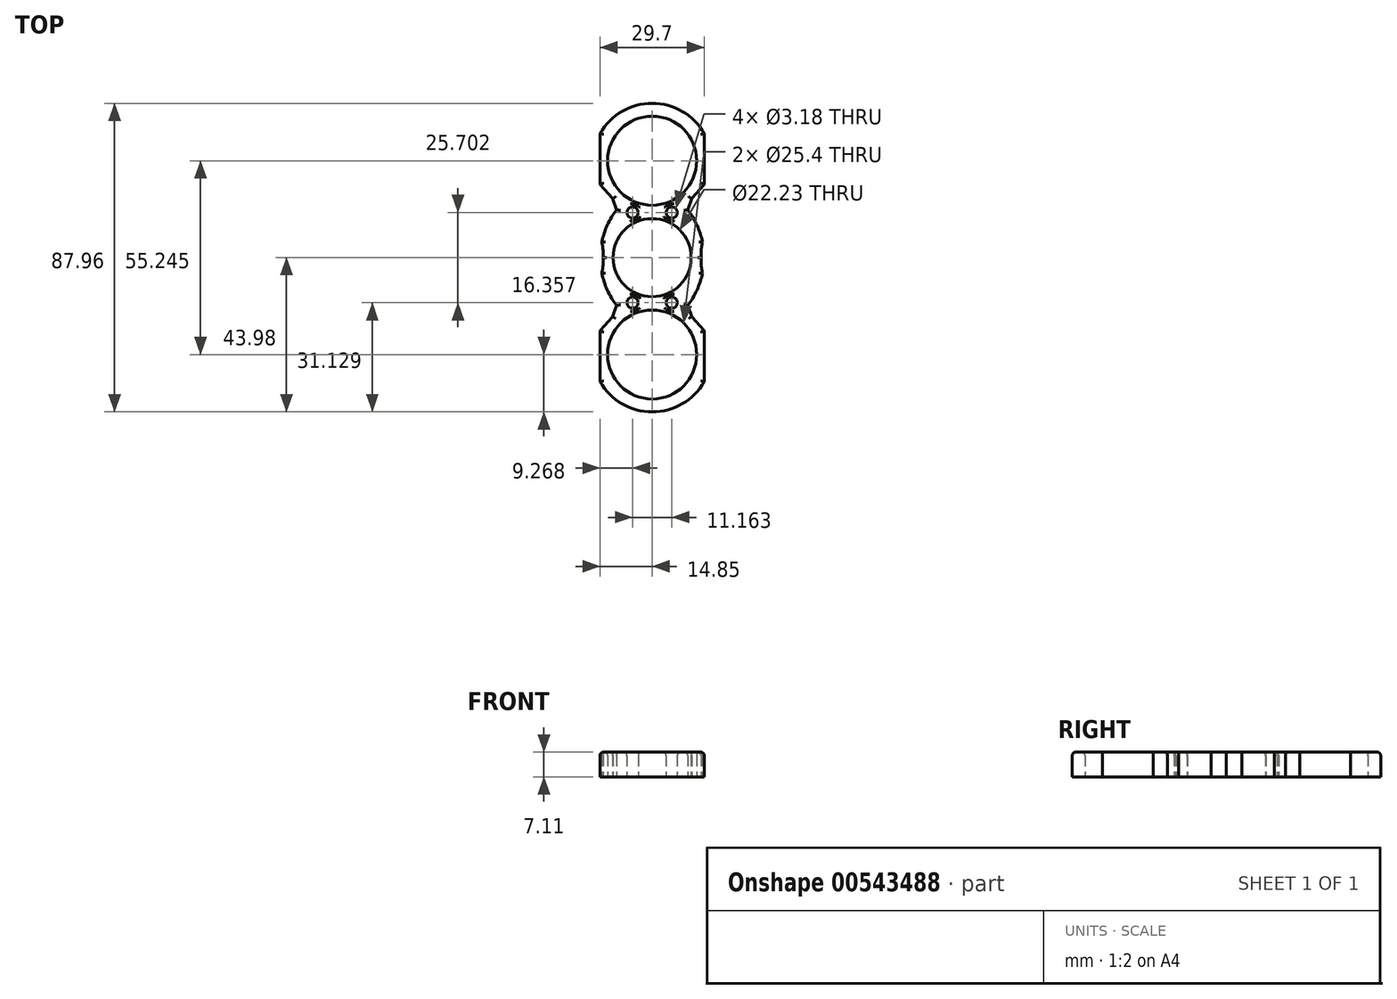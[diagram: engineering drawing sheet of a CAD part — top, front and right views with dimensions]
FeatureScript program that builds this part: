
annotation { "Feature Type Name" : "Feature", "Feature Type Description" : "" }
export const myFeature = defineFeature(function(context is Context, id is Id, definition is map)
    precondition{}
    {
        {
            var Q0;
            Q0=qCreatedBy(makeId("Top.planeOp"),FACE);
            var sketch = newSketch(context, id + "F0", { "sketchPlane" : qUnion([Q0])});
            skCircle(sketch, "E0", {"center": v(0, 0) * mm, "radius": 11.11 * mm});
            skCircle(sketch, "E1", {"center": v(0, 27.62) * mm, "radius": 12.7 * mm});
            skCircle(sketch, "E2", {"center": v(0, -27.62) * mm, "radius": 12.7 * mm});
            skLineSegment(sketch, "E3", {"start": v(-6, 42.55) * mm, "end": v(-5.71, 42.55) * mm});
            skLineSegment(sketch, "E4", {"start": v(14.85, 35.41) * mm, "end": v(14.85, 20.85) * mm});
            skLineSegment(sketch, "E5", {"start": v(14.85, 20.85) * mm, "end": v(11.28, 16.85) * mm});
            skLineSegment(sketch, "E6", {"start": v(-56.83, 0) * mm, "end": v(-12.8, 0) * mm});
            skLineSegment(sketch, "E7", {"start": v(0, 64.82) * mm, "end": v(0, -65.68) * mm});
            skLineSegment(sketch, "E8.MirrorCS", {"start": v(-6, -42.55) * mm, "end": v(-5.71, -42.55) * mm});
            skLineSegment(sketch, "E9.MirrorCS", {"start": v(14.85, -35.41) * mm, "end": v(14.85, -20.85) * mm});
            skLineSegment(sketch, "E10.MirrorCS", {"start": v(14.85, -20.85) * mm, "end": v(11.28, -16.85) * mm});
            skLineSegment(sketch, "E11.MirrorCS", {"start": v(-14.85, 35.41) * mm, "end": v(-14.85, 20.85) * mm});
            skLineSegment(sketch, "E12.MirrorCS", {"start": v(-14.85, 20.85) * mm, "end": v(-11.28, 16.85) * mm});
            skLineSegment(sketch, "E13.MirrorCS", {"start": v(-14.85, -20.85) * mm, "end": v(-11.28, -16.85) * mm});
            skLineSegment(sketch, "E14.MirrorCS", {"start": v(-14.85, -35.41) * mm, "end": v(-14.85, -20.85) * mm});
            skPoint(sketch, "E15.MirrorCS.end.orphan", {"position": v(-14.85, -35.41) * mm});
            skPoint(sketch, "E15.MirrorCS.start.orphan", {"position": v(-5.71, -42.55) * mm});
            skPoint(sketch, "E16.trimOffspring.end.orphan", {"position": v(5.71, -42.55) * mm});
            skPoint(sketch, "E17.MirrorCS.end.orphan", {"position": v(14.85, -35.41) * mm});
            skArc(sketch, "E18", {"start": v(-14.85, -35.41) * mm, "mid": v(0, -43.98) * mm, "end": v(14.85, -35.41) * mm});
            skPoint(sketch, "E19.MirrorCS.end.orphan", {"position": v(-14.85, 35.41) * mm});
            skPoint(sketch, "E19.MirrorCS.start.orphan", {"position": v(-5.71, 42.55) * mm});
            skPoint(sketch, "E20.start.orphan", {"position": v(5.71, 42.55) * mm});
            skArc(sketch, "E21.MirrorCS", {"start": v(-14.85, 35.41) * mm, "mid": v(0, 43.98) * mm, "end": v(14.85, 35.41) * mm});
            skPoint(sketch, "E22.orphan", {"position": v(-14.85, 0) * mm});
            skPoint(sketch, "E23.orphan", {"position": v(14.85, 0) * mm});
            skLineSegment(sketch, "E24", {"start": v(11.28, 16.85) * mm, "end": v(10.16, 13.64) * mm});
            skLineSegment(sketch, "E25.MirrorCS", {"start": v(-11.28, 16.85) * mm, "end": v(-10.16, 13.64) * mm});
            skPoint(sketch, "E26.orphan", {"position": v(-7.71, 12.85) * mm});
            skPoint(sketch, "E27.orphan", {"position": v(7.71, 12.85) * mm});
            skLineSegment(sketch, "E28.MirrorCS", {"start": v(-11.28, -16.85) * mm, "end": v(-10.16, -13.64) * mm});
            skLineSegment(sketch, "E29.MirrorCS", {"start": v(11.28, -16.85) * mm, "end": v(10.16, -13.64) * mm});
            skPoint(sketch, "E30.orphan", {"position": v(-7.71, -12.85) * mm});
            skPoint(sketch, "E31.orphan", {"position": v(7.71, -12.85) * mm});
            skCircle(sketch, "E32", {"center": v(-5.58, 12.85) * mm, "radius": 1.59 * mm});
            skCircle(sketch, "E33.MirrorC", {"center": v(-5.58, -12.85) * mm, "radius": 1.59 * mm});
            skCircle(sketch, "E34.MirrorC", {"center": v(5.58, 12.85) * mm, "radius": 1.59 * mm});
            skCircle(sketch, "E35.MirrorC", {"center": v(5.58, -12.85) * mm, "radius": 1.59 * mm});
            skPoint(sketch, "E36.orphan", {"position": v(-13.27, -35.21) * mm});
            skPoint(sketch, "E37.end.orphan", {"position": v(13.09, -35.41) * mm});
            skPoint(sketch, "E38.orphan", {"position": v(-13.27, 35.21) * mm});
            skPoint(sketch, "E39.MirrorCS.end.orphan", {"position": v(13.09, 35.41) * mm});
            skLineSegment(sketch, "E40.trimOffspring", {"start": v(-11.11, 0) * mm, "end": v(65.4, 0) * mm});
            skPoint(sketch, "E41.end.orphan", {"position": v(-12.8, -3.68) * mm});
            skPoint(sketch, "E42.MirrorCS.end.orphan", {"position": v(-12.8, 3.68) * mm});
            skPoint(sketch, "E43.orphan", {"position": v(12.8, -3.68) * mm});
            skPoint(sketch, "E44.end.orphan", {"position": v(12.8, 3.68) * mm});
            skArc(sketch, "E45", {"start": v(-10.16, 13.64) * mm, "mid": v(-12.78, 9.26) * mm, "end": v(-14.34, 4.4) * mm});
            skArc(sketch, "E46.MirrorCS", {"start": v(10.16, 13.64) * mm, "mid": v(12.78, 9.26) * mm, "end": v(14.34, 4.4) * mm});
            skPoint(sketch, "E47.orphan", {"position": v(-9.05, 10.44) * mm});
            skPoint(sketch, "E48.orphan", {"position": v(-9.05, -10.44) * mm});
            skPoint(sketch, "E49.orphan", {"position": v(9.05, -10.44) * mm});
            skPoint(sketch, "E50.MirrorCS.start.orphan", {"position": v(9.05, 10.44) * mm});
            skArc(sketch, "E51", {"start": v(-13.94, 0) * mm, "mid": v(-14.01, 2.21) * mm, "end": v(-14.34, 4.4) * mm});
            skArc(sketch, "E52.MirrorCS", {"start": v(-13.94, 0) * mm, "mid": v(-14.01, -2.21) * mm, "end": v(-14.34, -4.4) * mm});
            skArc(sketch, "E53.MirrorCS", {"start": v(13.94, 0) * mm, "mid": v(14.01, 2.21) * mm, "end": v(14.34, 4.4) * mm});
            skArc(sketch, "E54.MirrorCS", {"start": v(13.94, 0) * mm, "mid": v(14.01, -2.21) * mm, "end": v(14.34, -4.4) * mm});
            skArc(sketch, "E55.trimOffspring", {"start": v(-14.34, -4.4) * mm, "mid": v(-12.78, -9.26) * mm, "end": v(-10.16, -13.64) * mm});
            skArc(sketch, "E56.trimOffspring", {"start": v(14.34, -4.4) * mm, "mid": v(12.78, -9.26) * mm, "end": v(10.16, -13.64) * mm});
            skSolve(sketch);
        }
        {
            var Q0;
            {var subQ11=sQuery(id+"F0.wireOp",EDGE,"E11.MirrorCS");Q0=makeQuery(id+"F0.imprint","IMPRINT",FACE,{"disambiguationData":[TD([[makeQuery(id+"F0.imprint","IMPRINT",EDGE,{"derivedFrom":subQ11}),1.0]])]});}
            var Q1;
            {var subQ1=sQuery(id+"F0.wireOp",EDGE,"E4");Q1=makeQuery(id+"F0.imprint","IMPRINT",FACE,{"disambiguationData":[TD([[makeQuery(id+"F0.imprint","IMPRINT",EDGE,{"derivedFrom":subQ1}),-1.0]])]});}
            var Q2;
            {var subQ1=sQuery(id+"F0.wireOp",EDGE,"ecd911c1-05eb-48ea-925a-85692354c2d40.MirrorCS");Q2=makeQuery(id+"F0.imprint","IMPRINT",FACE,{"disambiguationData":[TD([[makeQuery(id+"F0.imprint","IMPRINT",EDGE,{"derivedFrom":subQ1}),-1.0]])]});}
            var Q3;
            {var subQ4=sQuery(id+"F0.wireOp",EDGE,"E9.MirrorCS");Q3=makeQuery(id+"F0.imprint","IMPRINT",FACE,{"disambiguationData":[TD([[makeQuery(id+"F0.imprint","IMPRINT",EDGE,{"derivedFrom":subQ4}),1.0]])]});}
            extrude(context, id + "F1", {"entities" : qUnion([Q0, Q1, Q2, Q3]), "depth" : 7.11 * mm, "offsetDistance" : 25.4 * mm});
        }
        {
            var Q0;
            Q0=makeQuery(id+"F1.opExtrude","CAP_EDGE",EDGE,{"disambiguationData":[OSD([sQuery(id+"F0.wireOp",EDGE,"E21.MirrorCS")])],"isStart":false});
            var Q1;
            Q1=makeQuery(id+"F1.opExtrude","CAP_EDGE",EDGE,{"disambiguationData":[OSD([sQuery(id+"F0.wireOp",EDGE,"E11.MirrorCS")])],"isStart":false});
            var Q2;
            Q2=makeQuery(id+"F1.opExtrude","CAP_EDGE",EDGE,{"disambiguationData":[OSD([sQuery(id+"F0.wireOp",EDGE,"E4")])],"isStart":false});
            var Q3;
            Q3=makeQuery(id+"F1.opExtrude","CAP_EDGE",EDGE,{"disambiguationData":[OSD([sQuery(id+"F0.wireOp",EDGE,"E12.MirrorCS")])],"isStart":false});
            var Q4;
            Q4=makeQuery(id+"F1.opExtrude","CAP_EDGE",EDGE,{"disambiguationData":[OSD([sQuery(id+"F0.wireOp",EDGE,"E25.MirrorCS")])],"isStart":false});
            var Q5;
            Q5=makeQuery(id+"F1.opExtrude","CAP_EDGE",EDGE,{"disambiguationData":[OSD([sQuery(id+"F0.wireOp",EDGE,"E42.MirrorCS")])],"isStart":false});
            var Q6;
            Q6=makeQuery(id+"F1.opExtrude","CAP_EDGE",EDGE,{"disambiguationData":[OSD([sQuery(id+"F0.wireOp",EDGE,"E24")])],"isStart":false});
            var Q7;
            Q7=makeQuery(id+"F1.opExtrude","CAP_EDGE",EDGE,{"disambiguationData":[OSD([sQuery(id+"F0.wireOp",EDGE,"E5")])],"isStart":false});
            var Q8;
            Q8=makeQuery(id+"F1.opExtrude","CAP_EDGE",EDGE,{"disambiguationData":[OSD([sQuery(id+"F0.wireOp",EDGE,"E44")])],"isStart":false});
            var Q9;
            Q9=makeQuery(id+"F1.opExtrude","CAP_EDGE",EDGE,{"disambiguationData":[OSD([sQuery(id+"F0.wireOp",EDGE,"481f827d-7c93-4f8f-ba0d-fe1300a66f5e0.MirrorCS")])],"isStart":false});
            var Q10;
            Q10=makeQuery(id+"F1.opExtrude","CAP_EDGE",EDGE,{"disambiguationData":[OSD([sQuery(id+"F0.wireOp",EDGE,"E41")])],"isStart":false});
            var Q11;
            Q11=makeQuery(id+"F1.opExtrude","CAP_EDGE",EDGE,{"disambiguationData":[OSD([sQuery(id+"F0.wireOp",EDGE,"ecd911c1-05eb-48ea-925a-85692354c2d40.MirrorCS")])],"isStart":false});
            var Q12;
            Q12=makeQuery(id+"F1.opExtrude","CAP_EDGE",EDGE,{"disambiguationData":[OSD([sQuery(id+"F0.wireOp",EDGE,"E28.MirrorCS")])],"isStart":false});
            var Q13;
            Q13=makeQuery(id+"F1.opExtrude","CAP_EDGE",EDGE,{"disambiguationData":[OSD([sQuery(id+"F0.wireOp",EDGE,"E13.MirrorCS")])],"isStart":false});
            var Q14;
            Q14=makeQuery(id+"F1.opExtrude","CAP_EDGE",EDGE,{"disambiguationData":[OSD([sQuery(id+"F0.wireOp",EDGE,"E14.MirrorCS")])],"isStart":false});
            var Q15;
            Q15=makeQuery(id+"F1.opExtrude","CAP_EDGE",EDGE,{"disambiguationData":[OSD([sQuery(id+"F0.wireOp",EDGE,"E29.MirrorCS")])],"isStart":false});
            var Q16;
            Q16=makeQuery(id+"F1.opExtrude","CAP_EDGE",EDGE,{"disambiguationData":[OSD([sQuery(id+"F0.wireOp",EDGE,"f6da66dd-6fcb-4a6b-93cb-794cc1521f9f0.MirrorCS")])],"isStart":false});
            var Q17;
            Q17=makeQuery(id+"F1.opExtrude","CAP_EDGE",EDGE,{"disambiguationData":[OSD([sQuery(id+"F0.wireOp",EDGE,"E10.MirrorCS")])],"isStart":false});
            var Q18;
            Q18=makeQuery(id+"F1.opExtrude","CAP_EDGE",EDGE,{"disambiguationData":[OSD([sQuery(id+"F0.wireOp",EDGE,"E9.MirrorCS")])],"isStart":false});
            var Q19;
            Q19=makeQuery(id+"F1.opExtrude","CAP_EDGE",EDGE,{"disambiguationData":[OSD([sQuery(id+"F0.wireOp",EDGE,"E18")])],"isStart":false});
            var Q20;
            Q20=makeQuery(id+"F1.opExtrude","CAP_EDGE",EDGE,{"disambiguationData":[OSD([sQuery(id+"F0.wireOp",EDGE,"E21.MirrorCS")])],"isStart":true});
            var Q21;
            Q21=makeQuery(id+"F1.opExtrude","CAP_EDGE",EDGE,{"disambiguationData":[OSD([sQuery(id+"F0.wireOp",EDGE,"E4")])],"isStart":true});
            var Q22;
            Q22=makeQuery(id+"F1.opExtrude","CAP_EDGE",EDGE,{"disambiguationData":[OSD([sQuery(id+"F0.wireOp",EDGE,"E11.MirrorCS")])],"isStart":true});
            var Q23;
            Q23=makeQuery(id+"F1.opExtrude","CAP_EDGE",EDGE,{"disambiguationData":[OSD([sQuery(id+"F0.wireOp",EDGE,"E12.MirrorCS")])],"isStart":true});
            var Q24;
            Q24=makeQuery(id+"F1.opExtrude","CAP_EDGE",EDGE,{"disambiguationData":[OSD([sQuery(id+"F0.wireOp",EDGE,"E25.MirrorCS")])],"isStart":true});
            var Q25;
            Q25=makeQuery(id+"F1.opExtrude","CAP_EDGE",EDGE,{"disambiguationData":[OSD([sQuery(id+"F0.wireOp",EDGE,"E42.MirrorCS")])],"isStart":true});
            var Q26;
            Q26=makeQuery(id+"F1.opExtrude","CAP_EDGE",EDGE,{"disambiguationData":[OSD([sQuery(id+"F0.wireOp",EDGE,"E41")])],"isStart":true});
            var Q27;
            Q27=makeQuery(id+"F1.opExtrude","CAP_EDGE",EDGE,{"disambiguationData":[OSD([sQuery(id+"F0.wireOp",EDGE,"ecd911c1-05eb-48ea-925a-85692354c2d40.MirrorCS")])],"isStart":true});
            var Q28;
            Q28=makeQuery(id+"F1.opExtrude","CAP_EDGE",EDGE,{"disambiguationData":[OSD([sQuery(id+"F0.wireOp",EDGE,"E28.MirrorCS")])],"isStart":true});
            var Q29;
            Q29=makeQuery(id+"F1.opExtrude","CAP_EDGE",EDGE,{"disambiguationData":[OSD([sQuery(id+"F0.wireOp",EDGE,"E13.MirrorCS")])],"isStart":true});
            var Q30;
            Q30=makeQuery(id+"F1.opExtrude","CAP_EDGE",EDGE,{"disambiguationData":[OSD([sQuery(id+"F0.wireOp",EDGE,"E14.MirrorCS")])],"isStart":true});
            var Q31;
            Q31=makeQuery(id+"F1.opExtrude","CAP_EDGE",EDGE,{"disambiguationData":[OSD([sQuery(id+"F0.wireOp",EDGE,"E18")])],"isStart":true});
            var Q32;
            Q32=makeQuery(id+"F1.opExtrude","CAP_EDGE",EDGE,{"disambiguationData":[OSD([sQuery(id+"F0.wireOp",EDGE,"E13.MirrorCS")])],"isStart":true});
            var Q33;
            Q33=makeQuery(id+"F1.opExtrude","CAP_EDGE",EDGE,{"disambiguationData":[OSD([sQuery(id+"F0.wireOp",EDGE,"E5")])],"isStart":true});
            var Q34;
            Q34=makeQuery(id+"F1.opExtrude","CAP_EDGE",EDGE,{"disambiguationData":[OSD([sQuery(id+"F0.wireOp",EDGE,"E24")])],"isStart":true});
            var Q35;
            Q35=makeQuery(id+"F1.opExtrude","CAP_EDGE",EDGE,{"disambiguationData":[OSD([sQuery(id+"F0.wireOp",EDGE,"E44")])],"isStart":true});
            var Q36;
            Q36=makeQuery(id+"F1.opExtrude","CAP_EDGE",EDGE,{"disambiguationData":[OSD([sQuery(id+"F0.wireOp",EDGE,"481f827d-7c93-4f8f-ba0d-fe1300a66f5e0.MirrorCS")])],"isStart":true});
            var Q37;
            Q37=makeQuery(id+"F1.opExtrude","CAP_EDGE",EDGE,{"disambiguationData":[OSD([sQuery(id+"F0.wireOp",EDGE,"f6da66dd-6fcb-4a6b-93cb-794cc1521f9f0.MirrorCS")])],"isStart":true});
            var Q38;
            Q38=makeQuery(id+"F1.opExtrude","CAP_EDGE",EDGE,{"disambiguationData":[OSD([sQuery(id+"F0.wireOp",EDGE,"E29.MirrorCS")])],"isStart":true});
            var Q39;
            Q39=makeQuery(id+"F1.opExtrude","CAP_EDGE",EDGE,{"disambiguationData":[OSD([sQuery(id+"F0.wireOp",EDGE,"E10.MirrorCS")])],"isStart":true});
            var Q40;
            Q40=makeQuery(id+"F1.opExtrude","CAP_EDGE",EDGE,{"disambiguationData":[OSD([sQuery(id+"F0.wireOp",EDGE,"E9.MirrorCS")])],"isStart":true});
            var Q41;
            Q41=makeQuery(id+"F1.opExtrude","CAP_EDGE",EDGE,{"disambiguationData":[OSD([sQuery(id+"F0.wireOp",EDGE,"E29.MirrorCS")])],"isStart":true});
            chamfer(context, id + "F2", {"entities" : qUnion([Q0, Q1, Q2, Q3, Q4, Q5, Q6, Q7, Q8, Q9, Q10, Q11, Q12, Q13, Q14, Q15, Q16, Q17, Q18, Q19, Q20, Q21, Q22, Q23, Q24, Q25, Q26, Q27, Q28, Q29, Q30, Q31, Q32, Q33, Q34, Q35, Q36, Q37, Q38, Q39, Q40, Q41]), "width" : 1.78 * mm, "tangentPropagation" : true});
        }
        {
            var Q0;
            Q0 = qSketchRegion(id + "F0", true);
            extrude(context, id + "F3", {"entities" : qUnion([Q0]), "operationType" : NewBodyOperationType.ADD, "depth" : 7.11 * mm, "offsetDistance" : 25.4 * mm});
        }
        {
            var Q0;
            Q0=makeQuery(id+"F3.opExtrude","CAP_EDGE",EDGE,{"disambiguationData":[OSD([sQuery(id+"F0.wireOp",EDGE,"E11.MirrorCS")])],"isStart":false});
            var Q1;
            Q1=makeQuery(id+"F3.opExtrude","CAP_EDGE",EDGE,{"disambiguationData":[OSD([sQuery(id+"F0.wireOp",EDGE,"E21.MirrorCS")])],"isStart":false});
            var Q2;
            Q2=makeQuery(id+"F3.opExtrude","CAP_EDGE",EDGE,{"disambiguationData":[OSD([sQuery(id+"F0.wireOp",EDGE,"E4")])],"isStart":false});
            var Q3;
            Q3=makeQuery(id+"F3.opExtrude","CAP_EDGE",EDGE,{"disambiguationData":[OSD([sQuery(id+"F0.wireOp",EDGE,"E5")])],"isStart":false});
            var Q4;
            Q4=makeQuery(id+"F3.opExtrude","CAP_EDGE",EDGE,{"disambiguationData":[OSD([sQuery(id+"F0.wireOp",EDGE,"E12.MirrorCS")])],"isStart":false});
            var Q5;
            Q5=makeQuery(id+"F1.opExtrude","CAP_EDGE",EDGE,{"disambiguationData":[OSD([sQuery(id+"F0.wireOp",EDGE,"E45")])],"isStart":false});
            var Q6;
            Q6=makeQuery(id+"F3.opExtrude","CAP_EDGE",EDGE,{"disambiguationData":[OSD([sQuery(id+"F0.wireOp",EDGE,"E25.MirrorCS")])],"isStart":false});
            var Q7;
            Q7=makeQuery(id+"F3.opExtrude","CAP_EDGE",EDGE,{"disambiguationData":[OSD([sQuery(id+"F0.wireOp",EDGE,"E24")])],"isStart":false});
            var Q8;
            Q8=makeQuery(id+"F1.opExtrude","CAP_EDGE",EDGE,{"disambiguationData":[OSD([sQuery(id+"F0.wireOp",EDGE,"E46.MirrorCS")])],"isStart":false});
            var Q9;
            {var subQ0=sQuery(id+"F0.wireOp",EDGE,"E56.trimOffspring");var subQ1=sQuery(id+"F0.wireOp",EDGE,"E55.trimOffspring");var subQ2=sQuery(id+"F0.wireOp",EDGE,"E54.MirrorCS");var subQ3=sQuery(id+"F0.wireOp",EDGE,"E53.MirrorCS");var subQ4=sQuery(id+"F0.wireOp",EDGE,"E52.MirrorCS");var subQ5=sQuery(id+"F0.wireOp",EDGE,"E51");var subQ6=sQuery(id+"F0.wireOp",EDGE,"E46.MirrorCS");var subQ7=sQuery(id+"F0.wireOp",EDGE,"E45");var subQ8=sQuery(id+"F0.wireOp",EDGE,"E35.MirrorC");var subQ9=sQuery(id+"F0.wireOp",EDGE,"E34.MirrorC");var subQ10=sQuery(id+"F0.wireOp",EDGE,"E33.MirrorC");var subQ11=sQuery(id+"F0.wireOp",EDGE,"E32");var subQ12=sQuery(id+"F0.wireOp",EDGE,"E29.MirrorCS");var subQ13=sQuery(id+"F0.wireOp",EDGE,"E28.MirrorCS");var subQ14=sQuery(id+"F0.wireOp",EDGE,"E25.MirrorCS");var subQ15=sQuery(id+"F0.wireOp",EDGE,"E24");var subQ16=sQuery(id+"F0.wireOp",EDGE,"E21.MirrorCS");var subQ17=sQuery(id+"F0.wireOp",EDGE,"E18");var subQ18=sQuery(id+"F0.wireOp",EDGE,"E14.MirrorCS");var subQ19=sQuery(id+"F0.wireOp",EDGE,"E13.MirrorCS");var subQ20=sQuery(id+"F0.wireOp",EDGE,"E12.MirrorCS");var subQ21=sQuery(id+"F0.wireOp",EDGE,"E11.MirrorCS");var subQ22=sQuery(id+"F0.wireOp",EDGE,"E10.MirrorCS");var subQ23=sQuery(id+"F0.wireOp",EDGE,"E9.MirrorCS");var subQ24=sQuery(id+"F0.wireOp",EDGE,"E5");var subQ25=sQuery(id+"F0.wireOp",EDGE,"E4");var subQ26=sQuery(id+"F0.wireOp",EDGE,"E2");var subQ27=sQuery(id+"F0.wireOp",EDGE,"E1");var subQ28=sQuery(id+"F0.wireOp",EDGE,"E0");Q9=makeQuery(id+"F3.boolean.opBoolean","MERGE",FACE,{"derivedFrom":[makeQuery(id+"F1.opExtrude","CAP_FACE",FACE,{"disambiguationData":[OSD([subQ28,subQ27,subQ26,subQ25,subQ24,subQ23,subQ22,subQ21,subQ20,subQ19,subQ18,subQ17,subQ16,subQ15,subQ14,subQ13,subQ12,subQ11,subQ10,subQ9,subQ8,subQ7,subQ6,subQ5,subQ4,subQ3,subQ2,subQ1,subQ0])],"isStart":false}),makeQuery(id+"F3.opExtrude","CAP_FACE",FACE,{"disambiguationData":[OSD([subQ28,subQ27,subQ26,subQ25,subQ24,subQ23,subQ22,subQ21,subQ20,subQ19,subQ18,subQ17,subQ16,subQ15,subQ14,subQ13,subQ12,subQ11,subQ10,subQ9,subQ8,subQ7,subQ6,subQ5,subQ4,subQ3,subQ2,subQ1,subQ0])],"isStart":false})]});}
            fillet(context, id + "F4", {"entities" : qUnion([Q0, Q1, Q2, Q3, Q4, Q5, Q6, Q7, Q8, Q9]), "radius" : 1.02 * mm, "tangentPropagation" : true, "allowEdgeOverflow" : false});
        }
    });
